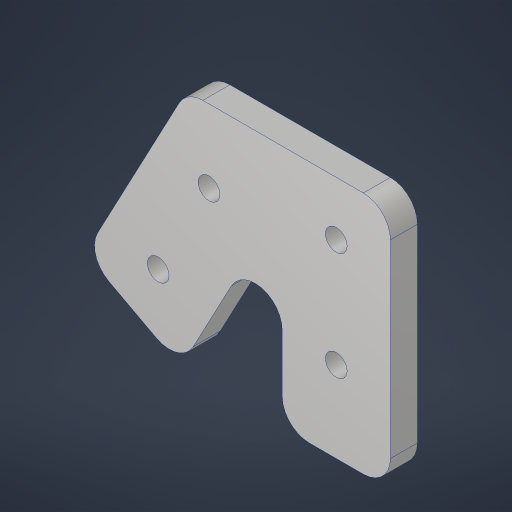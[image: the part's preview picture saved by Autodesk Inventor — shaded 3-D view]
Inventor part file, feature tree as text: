
AUTODESK INVENTOR PART (.ipt)
format: ipt  version: 2023.4 (Build 274418000, 418)  size: 205,824 bytes
history: native  units: in
note: dims shown in document units (in); Inventor stores cm internally (conversion verified against a paired STEP export)
features: sketch x1, extrude x1, hole x1, fillet x1
ambient origin geometry x8: Origin, YZ Plane, XZ Plane, XY Plane, X Axis, Y Axis, Z Axis, Center Point
bodies: Solid1 (feature_tree)
feature tree (4):
  sketch  "Sketch1"  dims[d0=1.0in d1=1.0in d2=0.1924in d3=2.0in d4=1.0in d5=0.5in d6=1.0in d7=0.5in d8=2.25in d9=0.25in d10=0.0in d11=0.201in d12=0.75in d13=0.385in d14=0.25in d15=0.5635in d16=1.0in d17=0.8108in d18=0.25in]
  extrude  "Extrusion1"  Depth=1.0in
  hole  "Hole1"  [1 undecoded]
  fillet  "Fillet1"  Radius=2.0in
note: 1 required parameter value undecoded (feature->parameter linkage not recoverable at this tier; creation-order binding heuristic only, values carry confidence <= 0.55)
